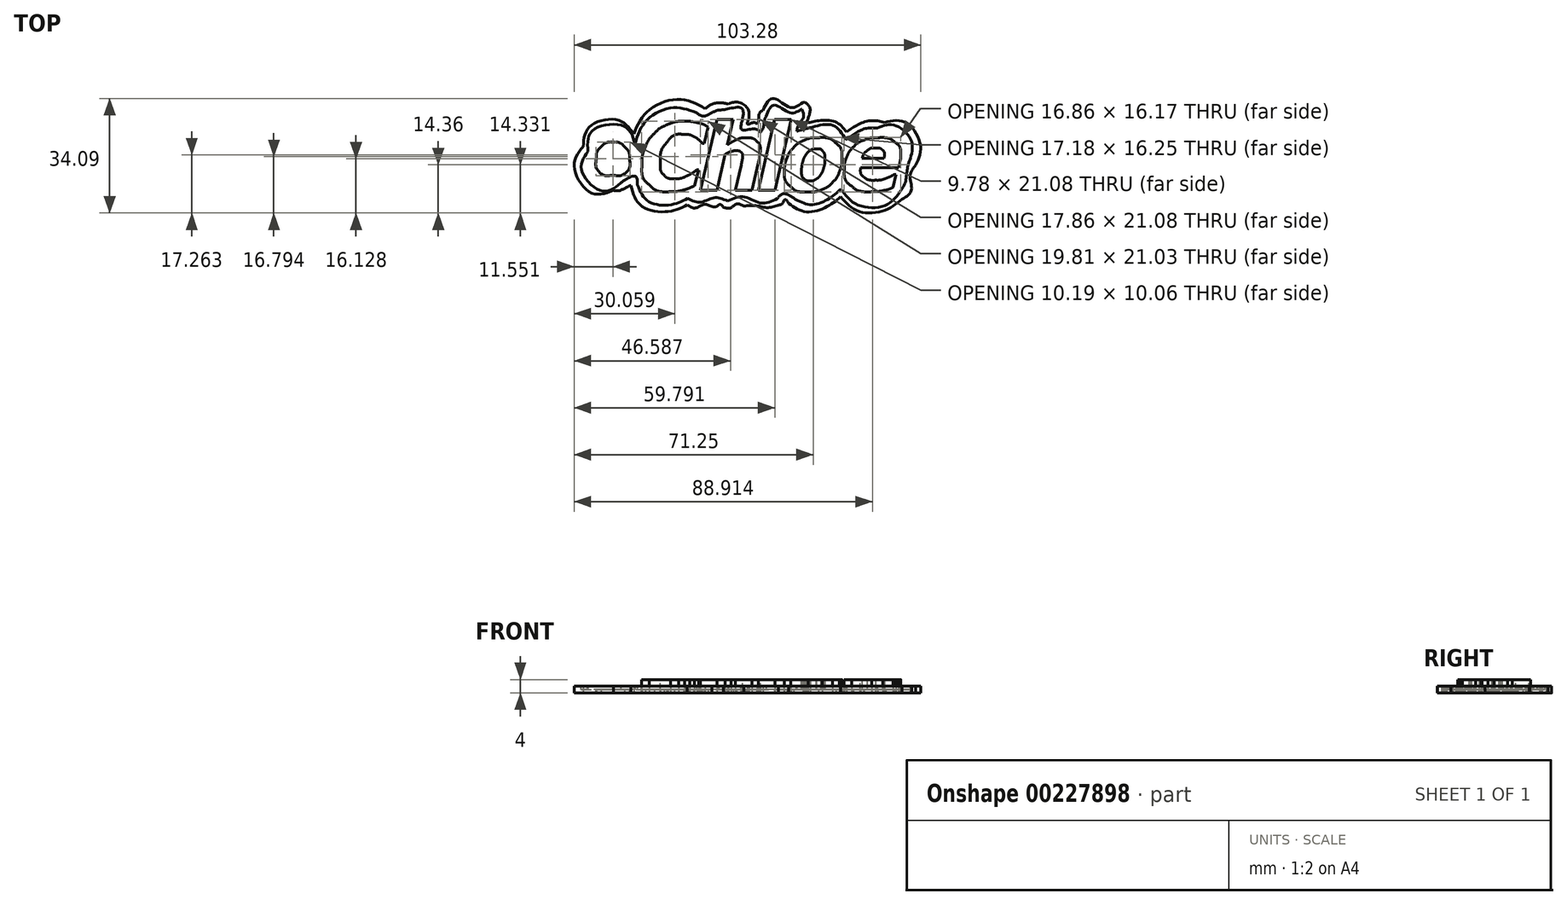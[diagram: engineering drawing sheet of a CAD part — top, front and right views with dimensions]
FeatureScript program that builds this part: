
annotation { "Feature Type Name" : "Feature", "Feature Type Description" : "" }
export const myFeature = defineFeature(function(context is Context, id is Id, definition is map)
    precondition{}
    {
        {
            var Q0;
            Q0=qCreatedBy(makeId("Top.planeOp"),FACE);
            var sketch = newSketch(context, id + "F0", { "sketchPlane" : qUnion([Q0])});
            skFitSpline(sketch, "E0", {"points": [v(-35.53, -1.12) * mm, v(-35.53, -3.84) * mm, v(-37.73, -6.05) * mm, v(-40.46, -6.05) * mm]});
            skFitSpline(sketch, "E1", {"points": [v(-40.46, -6.05) * mm, v(-43.18, -6.05) * mm, v(-45.4, -3.84) * mm, v(-45.4, -1.12) * mm]});
            skFitSpline(sketch, "E2", {"points": [v(-45.4, -1.12) * mm, v(-45.4, 0.19) * mm, v(-44.87, 1.44) * mm, v(-43.95, 2.37) * mm]});
            skFitSpline(sketch, "E3", {"points": [v(-43.95, 2.37) * mm, v(-43.02, 3.3) * mm, v(-41.77, 3.81) * mm, v(-40.46, 3.81) * mm]});
            skFitSpline(sketch, "E4", {"points": [v(-40.46, 3.81) * mm, v(-39.15, 3.81) * mm, v(-37.9, 3.3) * mm, v(-36.97, 2.37) * mm]});
            skFitSpline(sketch, "E5", {"points": [v(-36.97, 2.37) * mm, v(-36.05, 1.44) * mm, v(-35.53, 0.19) * mm, v(-35.53, -1.12) * mm]});
            skFitSpline(sketch, "E6", {"points": [v(-23.26, -10.98) * mm, v(-25.99, -10.98) * mm, v(-28.1, -10.3) * mm, v(-29.57, -8.97) * mm]});
            skFitSpline(sketch, "E7", {"points": [v(-29.57, -8.97) * mm, v(-31.05, -7.63) * mm, v(-31.8, -5.7) * mm, v(-31.8, -3.2) * mm]});
            skFitSpline(sketch, "E8", {"points": [v(-31.8, -3.2) * mm, v(-31.8, -1.22) * mm, v(-31.47, 0.57) * mm, v(-30.82, 2.17) * mm]});
            skFitSpline(sketch, "E9", {"points": [v(-30.82, 2.17) * mm, v(-30.16, 3.78) * mm, v(-29.26, 5.17) * mm, v(-28.11, 6.35) * mm]});
            skFitSpline(sketch, "E10", {"points": [v(-28.11, 6.35) * mm, v(-27, 7.48) * mm, v(-25.65, 8.37) * mm, v(-24.09, 9.01) * mm]});
            skFitSpline(sketch, "E11", {"points": [v(-24.09, 9.01) * mm, v(-22.52, 9.66) * mm, v(-20.87, 9.98) * mm, v(-19.14, 9.98) * mm]});
            skFitSpline(sketch, "E12", {"points": [v(-19.14, 9.98) * mm, v(-17.75, 9.98) * mm, v(-16.46, 9.83) * mm, v(-15.27, 9.54) * mm]});
            skFitSpline(sketch, "E13", {"points": [v(-15.27, 9.54) * mm, v(-14.08, 9.26) * mm, v(-13, 8.85) * mm, v(-12.05, 8.3) * mm]});
            skFitSpline(sketch, "E14", {"points": [v(-13.83, 3.4) * mm, v(-14.7, 4.33) * mm, v(-15.55, 5) * mm, v(-16.4, 5.44) * mm]});
            skFitSpline(sketch, "E15", {"points": [v(-16.4, 5.44) * mm, v(-17.24, 5.87) * mm, v(-18.24, 6.09) * mm, v(-19.39, 6.09) * mm]});
            skFitSpline(sketch, "E16", {"points": [v(-19.39, 6.09) * mm, v(-21.4, 6.09) * mm, v(-23.06, 5.28) * mm, v(-24.37, 3.66) * mm]});
            skFitSpline(sketch, "E17", {"points": [v(-24.37, 3.66) * mm, v(-25.67, 2.05) * mm, v(-26.32, -0.01) * mm, v(-26.32, -2.51) * mm]});
            skFitSpline(sketch, "E18", {"points": [v(-26.32, -2.51) * mm, v(-26.32, -4.12) * mm, v(-25.96, -5.28) * mm, v(-25.24, -6) * mm]});
            skFitSpline(sketch, "E19", {"points": [v(-25.24, -6) * mm, v(-24.52, -6.73) * mm, v(-23.46, -7.09) * mm, v(-22.07, -7.09) * mm]});
            skFitSpline(sketch, "E20", {"points": [v(-22.07, -7.09) * mm, v(-20.82, -7.09) * mm, v(-19.65, -6.84) * mm, v(-18.56, -6.34) * mm]});
            skFitSpline(sketch, "E21", {"points": [v(-18.56, -6.34) * mm, v(-17.47, -5.84) * mm, v(-16.44, -5.2) * mm, v(-15.46, -4.42) * mm]});
            skLineSegment(sketch, "E22", {"start": v(-12.05, 8.3) * mm, "end": v(-13.24, 3.4) * mm});
            skLineSegment(sketch, "E23", {"start": v(-13.24, 3.4) * mm, "end": v(-13.83, 3.4) * mm});
            skFitSpline(sketch, "E24", {"points": [v(-16.1, -9.24) * mm, v(-16.5, -9.4) * mm, v(-16.98, -9.6) * mm, v(-17.52, -9.84) * mm]});
            skFitSpline(sketch, "E25", {"points": [v(-17.52, -9.84) * mm, v(-18.06, -10.07) * mm, v(-18.58, -10.25) * mm, v(-19.08, -10.4) * mm]});
            skFitSpline(sketch, "E26", {"points": [v(-19.08, -10.4) * mm, v(-19.73, -10.58) * mm, v(-20.34, -10.73) * mm, v(-20.9, -10.83) * mm]});
            skFitSpline(sketch, "E27", {"points": [v(-20.9, -10.83) * mm, v(-21.46, -10.93) * mm, v(-22.25, -10.98) * mm, v(-23.26, -10.98) * mm]});
            skLineSegment(sketch, "E28", {"start": v(-15.46, -4.42) * mm, "end": v(-14.92, -4.42) * mm});
            skLineSegment(sketch, "E29", {"start": v(-14.92, -4.42) * mm, "end": v(-16.1, -9.24) * mm});
            skFitSpline(sketch, "E30", {"points": [v(3.47, 1.19) * mm, v(3.47, 0.97) * mm, v(3.46, 0.69) * mm, v(3.42, 0.35) * mm]});
            skFitSpline(sketch, "E31", {"points": [v(3.42, 0.35) * mm, v(3.38, 0) * mm, v(3.33, -0.34) * mm, v(3.24, -0.68) * mm]});
            skFitSpline(sketch, "E32", {"points": [v(-2.23, -3.04) * mm, v(-2.1, -2.46) * mm, v(-2, -1.97) * mm, v(-1.93, -1.58) * mm]});
            skFitSpline(sketch, "E33", {"points": [v(-1.93, -1.58) * mm, v(-1.86, -1.18) * mm, v(-1.82, -0.82) * mm, v(-1.82, -0.5) * mm]});
            skFitSpline(sketch, "E34", {"points": [v(-1.82, -0.5) * mm, v(-1.82, 0.1) * mm, v(-1.98, 0.53) * mm, v(-2.28, 0.8) * mm]});
            skFitSpline(sketch, "E35", {"points": [v(-2.28, 0.8) * mm, v(-2.58, 1.06) * mm, v(-3.13, 1.2) * mm, v(-3.92, 1.2) * mm]});
            skFitSpline(sketch, "E36", {"points": [v(-3.92, 1.2) * mm, v(-4.3, 1.2) * mm, v(-4.76, 1.11) * mm, v(-5.26, 0.94) * mm]});
            skFitSpline(sketch, "E37", {"points": [v(-5.26, 0.94) * mm, v(-5.77, 0.78) * mm, v(-6.33, 0.53) * mm, v(-6.96, 0.2) * mm]});
            skLineSegment(sketch, "E38", {"start": v(3.24, -0.68) * mm, "end": v(0.95, -10.58) * mm});
            skLineSegment(sketch, "E39", {"start": v(0.95, -10.58) * mm, "end": v(-3.98, -10.58) * mm});
            skLineSegment(sketch, "E40", {"start": v(-3.98, -10.58) * mm, "end": v(-2.23, -3.04) * mm});
            skFitSpline(sketch, "E41", {"points": [v(-6.32, 2.95) * mm, v(-5.33, 3.6) * mm, v(-4.41, 4.12) * mm, v(-3.58, 4.5) * mm]});
            skFitSpline(sketch, "E42", {"points": [v(-3.58, 4.5) * mm, v(-2.75, 4.86) * mm, v(-1.84, 5.05) * mm, v(-0.85, 5.05) * mm]});
            skFitSpline(sketch, "E43", {"points": [v(-0.85, 5.05) * mm, v(0.53, 5.05) * mm, v(1.6, 4.7) * mm, v(2.35, 4.03) * mm]});
            skFitSpline(sketch, "E44", {"points": [v(2.35, 4.03) * mm, v(3.1, 3.36) * mm, v(3.47, 2.41) * mm, v(3.47, 1.19) * mm]});
            skLineSegment(sketch, "E45", {"start": v(-6.96, 0.2) * mm, "end": v(-9.45, -10.58) * mm});
            skLineSegment(sketch, "E46", {"start": v(-9.45, -10.58) * mm, "end": v(-14.35, -10.58) * mm});
            skLineSegment(sketch, "E47", {"start": v(-14.35, -10.58) * mm, "end": v(-9.49, 10.5) * mm});
            skLineSegment(sketch, "E48", {"start": v(-9.49, 10.5) * mm, "end": v(-4.59, 10.5) * mm});
            skLineSegment(sketch, "E49", {"start": v(-4.59, 10.5) * mm, "end": v(-6.32, 2.95) * mm});
            skFitSpline(sketch, "E50", {"points": [v(21.44, -5.92) * mm, v(21.86, -5.3) * mm, v(22.17, -4.6) * mm, v(22.38, -3.85) * mm]});
            skFitSpline(sketch, "E51", {"points": [v(22.38, -3.85) * mm, v(22.6, -3.1) * mm, v(22.7, -2.2) * mm, v(22.7, -1.12) * mm]});
            skFitSpline(sketch, "E52", {"points": [v(22.7, -1.12) * mm, v(22.7, -0.19) * mm, v(22.5, 0.53) * mm, v(22.1, 1.02) * mm]});
            skFitSpline(sketch, "E53", {"points": [v(22.1, 1.02) * mm, v(21.69, 1.53) * mm, v(21.04, 1.78) * mm, v(20.15, 1.78) * mm]});
            skFitSpline(sketch, "E54", {"points": [v(20.15, 1.78) * mm, v(19.47, 1.78) * mm, v(18.86, 1.61) * mm, v(18.34, 1.28) * mm]});
            skFitSpline(sketch, "E55", {"points": [v(18.34, 1.28) * mm, v(17.82, 0.95) * mm, v(17.37, 0.47) * mm, v(16.97, -0.14) * mm]});
            skFitSpline(sketch, "E56", {"points": [v(16.97, -0.14) * mm, v(16.6, -0.71) * mm, v(16.3, -1.41) * mm, v(16.1, -2.25) * mm]});
            skFitSpline(sketch, "E57", {"points": [v(16.1, -2.25) * mm, v(15.88, -3.1) * mm, v(15.78, -3.96) * mm, v(15.78, -4.84) * mm]});
            skFitSpline(sketch, "E58", {"points": [v(15.78, -4.84) * mm, v(15.78, -5.88) * mm, v(16, -6.62) * mm, v(16.47, -7.08) * mm]});
            skFitSpline(sketch, "E59", {"points": [v(16.47, -7.08) * mm, v(16.93, -7.52) * mm, v(17.56, -7.74) * mm, v(18.37, -7.74) * mm]});
            skFitSpline(sketch, "E60", {"points": [v(18.37, -7.74) * mm, v(18.95, -7.74) * mm, v(19.52, -7.58) * mm, v(20.06, -7.27) * mm]});
            skFitSpline(sketch, "E61", {"points": [v(20.06, -7.27) * mm, v(20.6, -6.94) * mm, v(21.06, -6.5) * mm, v(21.44, -5.92) * mm]});
            skLineSegment(sketch, "E62", {"start": v(12.67, 10.5) * mm, "end": v(7.8, -10.58) * mm});
            skLineSegment(sketch, "E63", {"start": v(7.8, -10.58) * mm, "end": v(2.9, -10.58) * mm});
            skLineSegment(sketch, "E64", {"start": v(2.9, -10.58) * mm, "end": v(7.77, 10.5) * mm});
            skLineSegment(sketch, "E65", {"start": v(7.77, 10.5) * mm, "end": v(12.67, 10.5) * mm});
            skFitSpline(sketch, "E66", {"points": [v(27.78, -0.94) * mm, v(27.78, -2.37) * mm, v(27.54, -3.7) * mm, v(27.06, -4.95) * mm]});
            skFitSpline(sketch, "E67", {"points": [v(27.06, -4.95) * mm, v(26.58, -6.2) * mm, v(25.91, -7.27) * mm, v(25.04, -8.16) * mm]});
            skFitSpline(sketch, "E68", {"points": [v(25.04, -8.16) * mm, v(24.14, -9.09) * mm, v(23.1, -9.8) * mm, v(21.9, -10.31) * mm]});
            skFitSpline(sketch, "E69", {"points": [v(21.9, -10.31) * mm, v(20.7, -10.81) * mm, v(19.32, -11.06) * mm, v(17.73, -11.06) * mm]});
            skFitSpline(sketch, "E70", {"points": [v(17.73, -11.06) * mm, v(15.46, -11.06) * mm, v(13.73, -10.52) * mm, v(12.52, -9.43) * mm]});
            skFitSpline(sketch, "E71", {"points": [v(12.52, -9.43) * mm, v(11.3, -8.35) * mm, v(10.7, -6.85) * mm, v(10.7, -4.94) * mm]});
            skFitSpline(sketch, "E72", {"points": [v(10.7, -4.94) * mm, v(10.7, -3.58) * mm, v(10.93, -2.3) * mm, v(11.38, -1.08) * mm]});
            skFitSpline(sketch, "E73", {"points": [v(11.38, -1.08) * mm, v(11.83, 0.14) * mm, v(12.5, 1.22) * mm, v(13.38, 2.15) * mm]});
            skFitSpline(sketch, "E74", {"points": [v(13.38, 2.15) * mm, v(14.24, 3.06) * mm, v(15.3, 3.78) * mm, v(16.54, 4.3) * mm]});
            skFitSpline(sketch, "E75", {"points": [v(16.54, 4.3) * mm, v(17.8, 4.83) * mm, v(19.2, 5.1) * mm, v(20.75, 5.1) * mm]});
            skFitSpline(sketch, "E76", {"points": [v(20.75, 5.1) * mm, v(23.03, 5.1) * mm, v(24.76, 4.56) * mm, v(25.97, 3.49) * mm]});
            skFitSpline(sketch, "E77", {"points": [v(25.97, 3.49) * mm, v(27.18, 2.42) * mm, v(27.78, 0.95) * mm, v(27.78, -0.94) * mm]});
            skFitSpline(sketch, "E78", {"points": [v(36.64, -11) * mm, v(34.05, -11) * mm, v(32.05, -10.42) * mm, v(30.64, -9.27) * mm]});
            skFitSpline(sketch, "E79", {"points": [v(30.64, -9.27) * mm, v(29.24, -8.12) * mm, v(28.53, -6.54) * mm, v(28.53, -4.52) * mm]});
            skFitSpline(sketch, "E80", {"points": [v(28.53, -4.52) * mm, v(28.53, -3.13) * mm, v(28.76, -1.87) * mm, v(29.22, -0.71) * mm]});
            skFitSpline(sketch, "E81", {"points": [v(29.22, -0.71) * mm, v(29.68, 0.45) * mm, v(30.35, 1.46) * mm, v(31.21, 2.34) * mm]});
            skFitSpline(sketch, "E82", {"points": [v(31.21, 2.34) * mm, v(32.04, 3.19) * mm, v(33.08, 3.86) * mm, v(34.33, 4.36) * mm]});
            skFitSpline(sketch, "E83", {"points": [v(34.33, 4.36) * mm, v(35.57, 4.85) * mm, v(36.94, 5.1) * mm, v(38.43, 5.1) * mm]});
            skFitSpline(sketch, "E84", {"points": [v(38.43, 5.1) * mm, v(40.7, 5.1) * mm, v(42.4, 4.64) * mm, v(43.55, 3.72) * mm]});
            skFitSpline(sketch, "E85", {"points": [v(43.55, 3.72) * mm, v(44.7, 2.8) * mm, v(45.29, 1.46) * mm, v(45.29, -0.33) * mm]});
            skFitSpline(sketch, "E86", {"points": [v(45.29, -0.33) * mm, v(45.29, -0.95) * mm, v(45.22, -1.55) * mm, v(45.1, -2.13) * mm]});
            skFitSpline(sketch, "E87", {"points": [v(45.1, -2.13) * mm, v(44.98, -2.72) * mm, v(44.82, -3.3) * mm, v(44.62, -3.88) * mm]});
            skFitSpline(sketch, "E88", {"points": [v(33.33, -3.88) * mm, v(33.33, -3.93) * mm, v(33.33, -3.99) * mm, v(33.33, -4.04) * mm]});
            skFitSpline(sketch, "E89", {"points": [v(33.33, -4.04) * mm, v(33.33, -4.09) * mm, v(33.33, -4.14) * mm, v(33.33, -4.2) * mm]});
            skFitSpline(sketch, "E90", {"points": [v(33.33, -4.2) * mm, v(33.33, -5.25) * mm, v(33.7, -6.07) * mm, v(34.44, -6.67) * mm]});
            skFitSpline(sketch, "E91", {"points": [v(34.44, -6.67) * mm, v(35.18, -7.27) * mm, v(36.31, -7.56) * mm, v(37.84, -7.56) * mm]});
            skFitSpline(sketch, "E92", {"points": [v(37.84, -7.56) * mm, v(38.9, -7.56) * mm, v(39.9, -7.38) * mm, v(40.86, -7.02) * mm]});
            skFitSpline(sketch, "E93", {"points": [v(40.86, -7.02) * mm, v(41.81, -6.66) * mm, v(42.64, -6.26) * mm, v(43.35, -5.82) * mm]});
            skLineSegment(sketch, "E94", {"start": v(44.62, -3.88) * mm, "end": v(33.33, -3.88) * mm});
            skLineSegment(sketch, "E95", {"start": v(33.33, -3.88) * mm, "end": v(44.62, -3.88) * mm});
            skFitSpline(sketch, "E96", {"points": [v(42.98, -9.73) * mm, v(42.03, -10.15) * mm, v(41.04, -10.46) * mm, v(39.99, -10.67) * mm]});
            skFitSpline(sketch, "E97", {"points": [v(39.99, -10.67) * mm, v(38.94, -10.88) * mm, v(37.83, -11) * mm, v(36.64, -11) * mm]});
            skLineSegment(sketch, "E98", {"start": v(43.35, -5.82) * mm, "end": v(43.9, -5.82) * mm});
            skLineSegment(sketch, "E99", {"start": v(43.9, -5.82) * mm, "end": v(42.98, -9.73) * mm});
            skFitSpline(sketch, "E100", {"points": [v(40.37, -1.02) * mm, v(40.4, -0.86) * mm, v(40.41, -0.71) * mm, v(40.42, -0.57) * mm]});
            skFitSpline(sketch, "E101", {"points": [v(40.42, -0.57) * mm, v(40.44, -0.44) * mm, v(40.45, -0.3) * mm, v(40.45, -0.15) * mm]});
            skFitSpline(sketch, "E102", {"points": [v(40.45, -0.15) * mm, v(40.45, 0.56) * mm, v(40.23, 1.1) * mm, v(39.79, 1.48) * mm]});
            skFitSpline(sketch, "E103", {"points": [v(39.79, 1.48) * mm, v(39.34, 1.86) * mm, v(38.7, 2.05) * mm, v(37.88, 2.05) * mm]});
            skFitSpline(sketch, "E104", {"points": [v(37.88, 2.05) * mm, v(36.87, 2.05) * mm, v(36.03, 1.78) * mm, v(35.34, 1.24) * mm]});
            skFitSpline(sketch, "E105", {"points": [v(35.34, 1.24) * mm, v(34.67, 0.7) * mm, v(34.15, -0.06) * mm, v(33.8, -1.02) * mm]});
            skFitSpline(sketch, "E106", {"points": [v(16.16, 15.62) * mm, v(12.36, 14.12) * mm, v(7.32, 16.78) * mm, v(4.24, 13.25) * mm]});
            skFitSpline(sketch, "E107", {"points": [v(4.24, 13.25) * mm, v(3.11, 12.18) * mm, v(3.02, 10.28) * mm, v(2.56, 9.14) * mm]});
            skFitSpline(sketch, "E108", {"points": [v(2.56, 9.14) * mm, v(1.5, 9.63) * mm, v(-0.35, 9.1) * mm, v(0.05, 10.79) * mm]});
            skFitSpline(sketch, "E109", {"points": [v(0.05, 10.79) * mm, v(-0.24, 13.74) * mm, v(-3.19, 15.7) * mm, v(-6.03, 15.14) * mm]});
            skFitSpline(sketch, "E110", {"points": [v(-6.03, 15.14) * mm, v(-8.41, 15.51) * mm, v(-11.05, 15.04) * mm, v(-12.93, 13.75) * mm]});
            skFitSpline(sketch, "E111", {"points": [v(-12.93, 13.75) * mm, v(-20.67, 16.55) * mm, v(-30.1, 12.92) * mm, v(-34.25, 6.21) * mm]});
            skFitSpline(sketch, "E112", {"points": [v(-34.25, 6.21) * mm, v(-38.87, 10.33) * mm, v(-47.32, 8.46) * mm, v(-49.3, 2.43) * mm]});
            skFitSpline(sketch, "E113", {"points": [v(-49.3, 2.43) * mm, v(-52, -3.44) * mm, v(-46.97, -11.3) * mm, v(-40.34, -10.62) * mm]});
            skFitSpline(sketch, "E114", {"points": [v(-40.34, -10.62) * mm, v(-38.51, -10.66) * mm, v(-36.58, -9.78) * mm, v(-35.13, -9.11) * mm]});
            skFitSpline(sketch, "E115", {"points": [v(-35.13, -9.11) * mm, v(-32.12, -15.1) * mm, v(-24.26, -16.92) * mm, v(-18.26, -14.93) * mm]});
            skFitSpline(sketch, "E116", {"points": [v(-18.26, -14.93) * mm, v(-15.83, -15.84) * mm, v(-13.44, -14.8) * mm, v(-11.01, -15.36) * mm]});
            skFitSpline(sketch, "E117", {"points": [v(-11.01, -15.36) * mm, v(-9.73, -15.48) * mm, v(-8.58, -14.78) * mm, v(-7.48, -15.62) * mm]});
            skFitSpline(sketch, "E118", {"points": [v(-7.48, -15.62) * mm, v(-5.42, -15.82) * mm, v(-3.5, -14.61) * mm, v(-1.43, -15.27) * mm]});
            skFitSpline(sketch, "E119", {"points": [v(-1.43, -15.27) * mm, v(2, -15.13) * mm, v(5.54, -15.72) * mm, v(8.88, -14.97) * mm]});
            skFitSpline(sketch, "E120", {"points": [v(8.88, -14.97) * mm, v(9.97, -14.57) * mm, v(10.86, -13.34) * mm, v(11.93, -14.44) * mm]});
            skFitSpline(sketch, "E121", {"points": [v(11.93, -14.44) * mm, v(16.92, -16.97) * mm, v(23.18, -15.52) * mm, v(27.44, -12.51) * mm]});
            skFitSpline(sketch, "E122", {"points": [v(27.44, -12.51) * mm, v(32.49, -16.72) * mm, v(40.3, -16.59) * mm, v(45.75, -13.25) * mm]});
            skFitSpline(sketch, "E123", {"points": [v(45.75, -13.25) * mm, v(48.5, -10.56) * mm, v(48.13, -6.33) * mm, v(49.78, -3.06) * mm]});
            skFitSpline(sketch, "E124", {"points": [v(49.78, -3.06) * mm, v(51.2, 2.81) * mm, v(46.76, 9.62) * mm, v(40.48, 9.67) * mm]});
            skFitSpline(sketch, "E125", {"points": [v(40.48, 9.67) * mm, v(36.5, 10.18) * mm, v(32.46, 8.94) * mm, v(29.13, 6.78) * mm]});
            skFitSpline(sketch, "E126", {"points": [v(29.13, 6.78) * mm, v(26, 9.75) * mm, v(21.12, 10.18) * mm, v(17.2, 9.46) * mm]});
            skFitSpline(sketch, "E127", {"points": [v(17.2, 9.46) * mm, v(17.95, 11.47) * mm, v(18.27, 13.95) * mm, v(16.79, 15.74) * mm]});
            skLineSegment(sketch, "E128", {"start": v(33.8, -1.02) * mm, "end": v(40.37, -1.02) * mm});
            skLineSegment(sketch, "E129", {"start": v(40.37, -1.02) * mm, "end": v(40.37, -1.02) * mm});
            skLineSegment(sketch, "E130", {"start": v(40.37, -1.02) * mm, "end": v(33.8, -1.02) * mm});
            skFitSpline(sketch, "E131", {"points": [v(15.62, 13.52) * mm, v(12.26, 12.56) * mm, v(7.56, 14.8) * mm, v(5.21, 11.45) * mm]});
            skFitSpline(sketch, "E132", {"points": [v(5.21, 11.45) * mm, v(4.58, 9.9) * mm, v(4.4, 8.18) * mm, v(3.56, 6.7) * mm]});
            skFitSpline(sketch, "E133", {"points": [v(3.56, 6.7) * mm, v(1.72, 7.72) * mm, v(-2.01, 7.48) * mm, v(-1.85, 10.48) * mm]});
            skFitSpline(sketch, "E134", {"points": [v(-1.85, 10.48) * mm, v(-2.08, 13.91) * mm, v(-6.5, 13.61) * mm, v(-8.94, 13.34) * mm]});
            skFitSpline(sketch, "E135", {"points": [v(-8.94, 13.34) * mm, v(-11.06, 12.54) * mm, v(-13.33, 11.5) * mm, v(-15.57, 12.56) * mm]});
            skFitSpline(sketch, "E136", {"points": [v(-15.57, 12.56) * mm, v(-22.84, 14) * mm, v(-30.67, 9.98) * mm, v(-33.86, 3.25) * mm]});
            skFitSpline(sketch, "E137", {"points": [v(-33.86, 3.25) * mm, v(-37.18, 8.5) * mm, v(-46.54, 7.18) * mm, v(-47.88, 1) * mm]});
            skFitSpline(sketch, "E138", {"points": [v(-47.88, 1) * mm, v(-49.8, -4.48) * mm, v(-43.66, -10.8) * mm, v(-38.14, -8.41) * mm]});
            skFitSpline(sketch, "E139", {"points": [v(-38.14, -8.41) * mm, v(-36.64, -7.34) * mm, v(-33.73, -6.4) * mm, v(-33.1, -8.94) * mm]});
            skFitSpline(sketch, "E140", {"points": [v(-33.1, -8.94) * mm, v(-30.06, -13.75) * mm, v(-23.3, -14.9) * mm, v(-18.24, -12.98) * mm]});
            skFitSpline(sketch, "E141", {"points": [v(-18.24, -12.98) * mm, v(-14.35, -14.13) * mm, v(-10.22, -12.77) * mm, v(-6.3, -13.77) * mm]});
            skFitSpline(sketch, "E142", {"points": [v(-6.3, -13.77) * mm, v(-1.47, -12.5) * mm, v(3.73, -14.38) * mm, v(8.56, -13.02) * mm]});
            skFitSpline(sketch, "E143", {"points": [v(8.56, -13.02) * mm, v(10.22, -11.6) * mm, v(12.42, -12.26) * mm, v(14.02, -13.31) * mm]});
            skFitSpline(sketch, "E144", {"points": [v(14.02, -13.31) * mm, v(18.69, -14.85) * mm, v(23.82, -13.13) * mm, v(27.54, -10.18) * mm]});
            skFitSpline(sketch, "E145", {"points": [v(27.54, -10.18) * mm, v(32.06, -14.7) * mm, v(40.27, -15.25) * mm, v(45.1, -11.08) * mm]});
            skFitSpline(sketch, "E146", {"points": [v(45.1, -11.08) * mm, v(46.74, -7.97) * mm, v(47.24, -4.36) * mm, v(48.2, -1.03) * mm]});
            skFitSpline(sketch, "E147", {"points": [v(48.2, -1.03) * mm, v(48.48, 4.16) * mm, v(43.48, 8.83) * mm, v(38.29, 7.93) * mm]});
            skFitSpline(sketch, "E148", {"points": [v(38.29, 7.93) * mm, v(34.88, 7.83) * mm, v(31.66, 6.38) * mm, v(28.9, 4.45) * mm]});
            skFitSpline(sketch, "E149", {"points": [v(28.9, 4.45) * mm, v(25.33, 8.68) * mm, v(19.2, 8.34) * mm, v(14.34, 7.01) * mm]});
            skFitSpline(sketch, "E150", {"points": [v(14.34, 7.01) * mm, v(14.98, 9.13) * mm, v(16.36, 11.29) * mm, v(15.86, 13.58) * mm]});
            skLineSegment(sketch, "E151", {"start": v(16.79, 15.74) * mm, "end": v(16.33, 15.65) * mm});
            skLineSegment(sketch, "E152", {"start": v(16.33, 15.65) * mm, "end": v(16.16, 15.62) * mm});
            skLineSegment(sketch, "E153", {"start": v(16.16, 15.62) * mm, "end": v(16.79, 15.74) * mm});
            skLineSegment(sketch, "E154", {"start": v(15.86, 13.58) * mm, "end": v(15.62, 13.52) * mm});
            skLineSegment(sketch, "E155", {"start": v(15.62, 13.52) * mm, "end": v(15.86, 13.58) * mm});
            skSolve(sketch);
        }
        {
            var Q0;
            Q0=makeQuery(id+"F0.imprint","IMPRINT",FACE,{"disambiguationData":[TD([[makeQuery(id+"F0.imprint","IMPRINT",EDGE,{"derivedFrom":sQuery(id+"F0.wireOp",EDGE,"E6")}),-1.0]])]});
            var Q1;
            Q1=makeQuery(id+"F0.imprint","IMPRINT",FACE,{"disambiguationData":[TD([[makeQuery(id+"F0.imprint","IMPRINT",EDGE,{"derivedFrom":sQuery(id+"F0.wireOp",EDGE,"E30")}),-1.0]])]});
            var Q2;
            Q2=makeQuery(id+"F0.imprint","IMPRINT",FACE,{"disambiguationData":[TD([[makeQuery(id+"F0.imprint","IMPRINT",EDGE,{"derivedFrom":sQuery(id+"F0.wireOp",EDGE,"E62")}),-1.0]])]});
            var Q3;
            Q3=makeQuery(id+"F0.imprint","IMPRINT",FACE,{"disambiguationData":[TD([[makeQuery(id+"F0.imprint","IMPRINT",EDGE,{"derivedFrom":sQuery(id+"F0.wireOp",EDGE,"E50")}),-1.0]])]});
            var Q4;
            Q4=makeQuery(id+"F0.imprint","IMPRINT",FACE,{"disambiguationData":[TD([[makeQuery(id+"F0.imprint","IMPRINT",EDGE,{"derivedFrom":sQuery(id+"F0.wireOp",EDGE,"E78")}),-1.0]])]});
            extrude(context, id + "F1", {"entities" : qUnion([Q0, Q1, Q2, Q3, Q4]), "depth" : 4 * mm});
        }
        {
            var Q0;
            Q0=makeQuery(id+"F0.imprint","IMPRINT",FACE,{"disambiguationData":[TD([[makeQuery(id+"F0.imprint","IMPRINT",EDGE,{"derivedFrom":sQuery(id+"F0.wireOp",EDGE,"E0")}),1.0]])]});
            extrude(context, id + "F2", {"entities" : qUnion([Q0]), "depth" : 1 * mm});
        }
        {
            var Q0;
            Q0=makeQuery(id+"F0.imprint","IMPRINT",FACE,{"disambiguationData":[TD([[makeQuery(id+"F0.imprint","IMPRINT",EDGE,{"derivedFrom":sQuery(id+"F0.wireOp",EDGE,"E106")}),1.0]])]});
            extrude(context, id + "F3", {"entities" : qUnion([Q0]), "operationType" : NewBodyOperationType.ADD, "depth" : 2 * mm});
        }
        {
            var Q0;
            Q0=makeQuery(id+"F0.imprint","IMPRINT",FACE,{"disambiguationData":[TD([[makeQuery(id+"F0.imprint","IMPRINT",EDGE,{"derivedFrom":sQuery(id+"F0.wireOp",EDGE,"E100")}),1.0]])]});
            var Q1;
            Q1=makeQuery(id+"F0.imprint","IMPRINT",FACE,{"disambiguationData":[TD([[makeQuery(id+"F0.imprint","IMPRINT",EDGE,{"derivedFrom":sQuery(id+"F0.wireOp",EDGE,"E50")}),1.0]])]});
            extrude(context, id + "F4", {"entities" : qUnion([Q0, Q1]), "operationType" : NewBodyOperationType.ADD, "depth" : 1 * mm});
        }
    });
